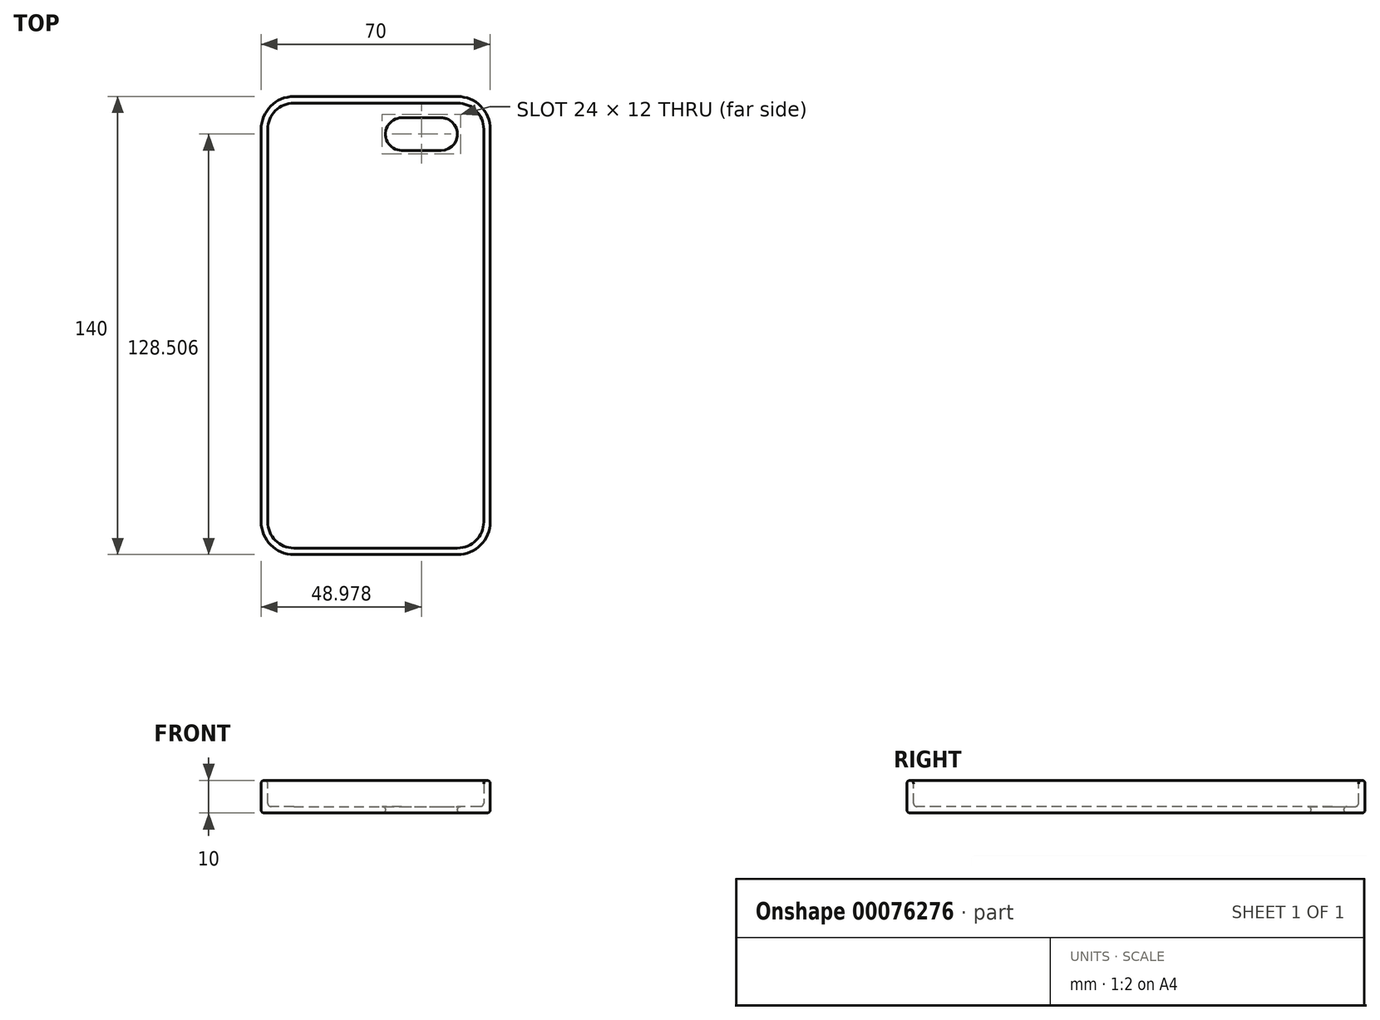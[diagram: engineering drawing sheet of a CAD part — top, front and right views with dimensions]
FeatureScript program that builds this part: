
annotation { "Feature Type Name" : "Feature", "Feature Type Description" : "" }
export const myFeature = defineFeature(function(context is Context, id is Id, definition is map)
    precondition{}
    {
        {
            var Q0;
            Q0=qCreatedBy(makeId("Top.planeOp"),FACE);
            var sketch = newSketch(context, id + "F0", { "sketchPlane" : qUnion([Q0])});
            skLineSegment(sketch, "E0.bottom", {"start": v(-23.57, 70.85) * mm, "end": v(26.43, 70.85) * mm});
            skLineSegment(sketch, "E0.top", {"start": v(-23.57, -69.15) * mm, "end": v(26.43, -69.15) * mm});
            skLineSegment(sketch, "E0.left", {"start": v(-33.57, 60.85) * mm, "end": v(-33.57, -59.15) * mm});
            skLineSegment(sketch, "E0.right", {"start": v(36.43, 60.85) * mm, "end": v(36.43, -59.15) * mm});
            skLineSegment(sketch, "E1.bottom", {"start": v(9.4, 64.36) * mm, "end": v(21.4, 64.36) * mm});
            skLineSegment(sketch, "E1.top", {"start": v(9.4, 54.36) * mm, "end": v(21.4, 54.36) * mm});
            skLineSegment(sketch, "E1.left", {"start": v(4.4, 59.36) * mm, "end": v(4.4, 59.36) * mm});
            skLineSegment(sketch, "E1.right", {"start": v(26.4, 59.36) * mm, "end": v(26.4, 59.36) * mm});
            skLineSegment(sketch, "E2.0", {"start": v(-23.38, 68.85) * mm, "end": v(26.84, 68.85) * mm});
            skLineSegment(sketch, "E3.0", {"start": v(-31.57, 60.76) * mm, "end": v(-31.57, -59.38) * mm});
            skLineSegment(sketch, "E4.0", {"start": v(-23.6, -67.15) * mm, "end": v(26.43, -67.15) * mm});
            skLineSegment(sketch, "E5.0", {"start": v(34.43, 60.88) * mm, "end": v(34.43, -59.15) * mm});
            skPoint(sketch, "E6.visualSharp", {"position": v(-33.57, 70.85) * mm});
            skArc(sketch, "E6.filletArc", {"start": v(-23.57, 70.85) * mm, "mid": v(-30.64, 67.92) * mm, "end": v(-33.57, 60.85) * mm});
            skPoint(sketch, "E7.visualSharp", {"position": v(36.43, 70.85) * mm});
            skArc(sketch, "E7.filletArc", {"start": v(36.43, 60.85) * mm, "mid": v(33.5, 67.92) * mm, "end": v(26.43, 70.85) * mm});
            skPoint(sketch, "E8.visualSharp", {"position": v(36.43, -69.15) * mm});
            skArc(sketch, "E8.filletArc", {"start": v(26.43, -69.15) * mm, "mid": v(33.5, -66.22) * mm, "end": v(36.43, -59.15) * mm});
            skPoint(sketch, "E9.visualSharp", {"position": v(-33.57, -69.15) * mm});
            skArc(sketch, "E9.filletArc", {"start": v(-33.57, -59.15) * mm, "mid": v(-30.64, -66.22) * mm, "end": v(-23.57, -69.15) * mm});
            skPoint(sketch, "E10.visualSharp", {"position": v(4.4, 54.36) * mm});
            skArc(sketch, "E10.filletArc", {"start": v(4.4, 59.36) * mm, "mid": v(5.87, 55.82) * mm, "end": v(9.4, 54.36) * mm});
            skPoint(sketch, "E11.visualSharp", {"position": v(4.4, 64.36) * mm});
            skArc(sketch, "E11.filletArc", {"start": v(9.4, 64.36) * mm, "mid": v(5.87, 62.9) * mm, "end": v(4.4, 59.36) * mm});
            skPoint(sketch, "E12.visualSharp", {"position": v(26.4, 64.36) * mm});
            skArc(sketch, "E12.filletArc", {"start": v(26.4, 59.36) * mm, "mid": v(24.94, 62.9) * mm, "end": v(21.4, 64.36) * mm});
            skPoint(sketch, "E13.visualSharp", {"position": v(26.4, 54.36) * mm});
            skArc(sketch, "E13.filletArc", {"start": v(21.4, 54.36) * mm, "mid": v(24.94, 55.82) * mm, "end": v(26.4, 59.36) * mm});
            skSolve(sketch);
        }
        {
            var Q0;
            Q0=makeQuery(id+"F0.imprint","IMPRINT",FACE,{"disambiguationData":[TD([[makeQuery(id+"F0.imprint","IMPRINT",EDGE,{"derivedFrom":sQuery(id+"F0.wireOp",EDGE,"E1.bottom")}),1.0]])]});
            extrude(context, id + "F1", {"entities" : qUnion([Q0]), "depth" : 2 * mm});
        }
        {
            var Q0;
            {var subQ0=sQuery(id+"F0.wireOp",EDGE,"E0.left");var subQ1=sQuery(id+"F0.wireOp",EDGE,"E0.bottom");var subQ2=makeQuery(id+"F0.imprint","INTERSECT",VERTEX,{"derivedFrom":[subQ1,subQ0]});Q0=makeQuery(id+"F0.imprint","IMPRINT",FACE,{"disambiguationData":[TD([[makeQuery(id+"F0.imprint","IMPRINT",EDGE,{"disambiguationData":[TD([[subQ2,-1.0]])],"derivedFrom":subQ1}),-1.0]])]});}
            var Q1;
            {var subQ0=sQuery(id+"F0.wireOp",EDGE,"E3.0");var subQ1=sQuery(id+"F0.wireOp",EDGE,"E0.bottom");var subQ2=makeQuery(id+"F0.imprint","INTERSECT",VERTEX,{"derivedFrom":[subQ1,subQ0]});Q1=makeQuery(id+"F0.imprint","IMPRINT",FACE,{"disambiguationData":[TD([[makeQuery(id+"F0.imprint","IMPRINT",EDGE,{"disambiguationData":[TD([[subQ2,-1.0]])],"derivedFrom":subQ1}),-1.0]])]});}
            var Q2;
            {var subQ0=sQuery(id+"F0.wireOp",EDGE,"E2.0");var subQ1=sQuery(id+"F0.wireOp",EDGE,"E0.left");var subQ2=makeQuery(id+"F0.imprint","INTERSECT",VERTEX,{"derivedFrom":[subQ1,subQ0]});Q2=makeQuery(id+"F0.imprint","IMPRINT",FACE,{"disambiguationData":[TD([[makeQuery(id+"F0.imprint","IMPRINT",EDGE,{"disambiguationData":[TD([[subQ2,-1.0]])],"derivedFrom":subQ1}),1.0]])]});}
            var Q3;
            {var subQ0=sQuery(id+"F0.wireOp",EDGE,"E0.left");var subQ1=sQuery(id+"F0.wireOp",EDGE,"E0.top");var subQ2=makeQuery(id+"F0.imprint","INTERSECT",VERTEX,{"derivedFrom":[subQ1,subQ0]});Q3=makeQuery(id+"F0.imprint","IMPRINT",FACE,{"disambiguationData":[TD([[makeQuery(id+"F0.imprint","IMPRINT",EDGE,{"disambiguationData":[TD([[subQ2,-1.0]])],"derivedFrom":subQ1}),1.0]])]});}
            var Q4;
            {var subQ0=sQuery(id+"F0.wireOp",EDGE,"E3.0");var subQ1=sQuery(id+"F0.wireOp",EDGE,"E0.top");var subQ2=makeQuery(id+"F0.imprint","INTERSECT",VERTEX,{"derivedFrom":[subQ1,subQ0]});Q4=makeQuery(id+"F0.imprint","IMPRINT",FACE,{"disambiguationData":[TD([[makeQuery(id+"F0.imprint","IMPRINT",EDGE,{"disambiguationData":[TD([[subQ2,-1.0]])],"derivedFrom":subQ1}),1.0]])]});}
            var Q5;
            {var subQ0=sQuery(id+"F0.wireOp",EDGE,"E2.0");var subQ1=sQuery(id+"F0.wireOp",EDGE,"E0.right");var subQ2=makeQuery(id+"F0.imprint","INTERSECT",VERTEX,{"derivedFrom":[subQ1,subQ0]});Q5=makeQuery(id+"F0.imprint","IMPRINT",FACE,{"disambiguationData":[TD([[makeQuery(id+"F0.imprint","IMPRINT",EDGE,{"disambiguationData":[TD([[subQ2,-1.0]])],"derivedFrom":subQ1}),-1.0]])]});}
            var Q6;
            {var subQ0=sQuery(id+"F0.wireOp",EDGE,"E0.right");var subQ1=sQuery(id+"F0.wireOp",EDGE,"E0.top");var subQ2=makeQuery(id+"F0.imprint","INTERSECT",VERTEX,{"derivedFrom":[subQ1,subQ0]});Q6=makeQuery(id+"F0.imprint","IMPRINT",FACE,{"disambiguationData":[TD([[makeQuery(id+"F0.imprint","IMPRINT",EDGE,{"disambiguationData":[TD([[subQ2,1.0]])],"derivedFrom":subQ1}),1.0]])]});}
            var Q7;
            {var subQ0=sQuery(id+"F0.wireOp",EDGE,"E0.right");var subQ1=sQuery(id+"F0.wireOp",EDGE,"E0.bottom");var subQ2=makeQuery(id+"F0.imprint","INTERSECT",VERTEX,{"derivedFrom":[subQ1,subQ0]});Q7=makeQuery(id+"F0.imprint","IMPRINT",FACE,{"disambiguationData":[TD([[makeQuery(id+"F0.imprint","IMPRINT",EDGE,{"disambiguationData":[TD([[subQ2,1.0]])],"derivedFrom":subQ1}),-1.0]])]});}
            extrude(context, id + "F2", {"entities" : qUnion([Q0, Q1, Q2, Q3, Q4, Q5, Q6, Q7]), "operationType" : NewBodyOperationType.ADD, "depth" : 10 * mm});
        }
        {
            var Q0;
            Q0=makeQuery(id+"F2.opExtrude","CAP_EDGE",EDGE,{"disambiguationData":[OSD([sQuery(id+"F0.wireOp",EDGE,"E0.left")])],"isStart":false});
            var Q1;
            Q1=makeQuery(id+"F2.opExtrude","CAP_EDGE",EDGE,{"disambiguationData":[OSD([sQuery(id+"F0.wireOp",EDGE,"E3.0")])],"isStart":false});
            var Q2;
            Q2=makeQuery(id+"F2.opExtrude","CAP_EDGE",EDGE,{"disambiguationData":[OSD([sQuery(id+"F0.wireOp",EDGE,"E2.0")])],"isStart":false});
            var Q3;
            Q3=makeQuery(id+"F2.opExtrude","CAP_EDGE",EDGE,{"disambiguationData":[OSD([sQuery(id+"F0.wireOp",EDGE,"E0.bottom")])],"isStart":false});
            var Q4;
            Q4=makeQuery(id+"F1.opExtrude","CAP_EDGE",EDGE,{"disambiguationData":[OSD([sQuery(id+"F0.wireOp",EDGE,"E1.bottom")])],"isStart":false});
            var Q5;
            Q5=makeQuery(id+"F1.opExtrude","CAP_EDGE",EDGE,{"disambiguationData":[OSD([sQuery(id+"F0.wireOp",EDGE,"E1.left")])],"isStart":false});
            var Q6;
            Q6=makeQuery(id+"F1.opExtrude","CAP_EDGE",EDGE,{"disambiguationData":[OSD([sQuery(id+"F0.wireOp",EDGE,"E1.right")])],"isStart":false});
            var Q7;
            Q7=makeQuery(id+"F1.opExtrude","CAP_EDGE",EDGE,{"disambiguationData":[OSD([sQuery(id+"F0.wireOp",EDGE,"E1.top")])],"isStart":false});
            var Q8;
            Q8=makeQuery(id+"F2.opExtrude","CAP_EDGE",EDGE,{"disambiguationData":[OSD([sQuery(id+"F0.wireOp",EDGE,"E5.0")])],"isStart":false});
            var Q9;
            Q9=makeQuery(id+"F2.opExtrude","CAP_EDGE",EDGE,{"disambiguationData":[OSD([sQuery(id+"F0.wireOp",EDGE,"E0.right")])],"isStart":false});
            var Q10;
            Q10=makeQuery(id+"F2.opExtrude","CAP_EDGE",EDGE,{"disambiguationData":[OSD([sQuery(id+"F0.wireOp",EDGE,"E4.0")])],"isStart":false});
            var Q11;
            Q11=makeQuery(id+"F2.opExtrude","CAP_EDGE",EDGE,{"disambiguationData":[OSD([sQuery(id+"F0.wireOp",EDGE,"E0.top")])],"isStart":false});
            fillet(context, id + "F3", {"entities" : qUnion([Q0, Q1, Q2, Q3, Q4, Q5, Q6, Q7, Q8, Q9, Q10, Q11]), "radius" : 1 * mm, "tangentPropagation" : true, "allowEdgeOverflow" : false});
        }
        {
            var Q0;
            Q0=makeQuery(id+"F2.opExtrude","CAP_EDGE",EDGE,{"disambiguationData":[OSD([sQuery(id+"F0.wireOp",EDGE,"E0.left")])],"isStart":true});
            var Q1;
            Q1=makeQuery(id+"F2.opExtrude","CAP_EDGE",EDGE,{"disambiguationData":[OSD([sQuery(id+"F0.wireOp",EDGE,"E0.top")])],"isStart":true});
            var Q2;
            Q2=makeQuery(id+"F2.opExtrude","CAP_EDGE",EDGE,{"disambiguationData":[OSD([sQuery(id+"F0.wireOp",EDGE,"E0.right")])],"isStart":true});
            var Q3;
            Q3=makeQuery(id+"F2.opExtrude","CAP_EDGE",EDGE,{"disambiguationData":[OSD([sQuery(id+"F0.wireOp",EDGE,"E0.bottom")])],"isStart":true});
            var Q4;
            Q4=makeQuery(id+"F1.opExtrude","CAP_EDGE",EDGE,{"disambiguationData":[OSD([sQuery(id+"F0.wireOp",EDGE,"E1.top")])],"isStart":true});
            var Q5;
            Q5=makeQuery(id+"F1.opExtrude","CAP_EDGE",EDGE,{"disambiguationData":[OSD([sQuery(id+"F0.wireOp",EDGE,"E1.left")])],"isStart":true});
            var Q6;
            Q6=makeQuery(id+"F1.opExtrude","CAP_EDGE",EDGE,{"disambiguationData":[OSD([sQuery(id+"F0.wireOp",EDGE,"E1.right")])],"isStart":true});
            var Q7;
            Q7=makeQuery(id+"F1.opExtrude","CAP_EDGE",EDGE,{"disambiguationData":[OSD([sQuery(id+"F0.wireOp",EDGE,"E1.bottom")])],"isStart":true});
            fillet(context, id + "F4", {"entities" : qUnion([Q0, Q1, Q2, Q3, Q4, Q5, Q6, Q7]), "radius" : 1 * mm, "tangentPropagation" : true, "allowEdgeOverflow" : false});
        }
        {
            var Q0;
            {var subQ0=sQuery(id+"F0.wireOp",EDGE,"E11.filletArc");var subQ1=sQuery(id+"F0.wireOp",EDGE,"E10.filletArc");Q0=makeQuery(id+"F2.boolean.opBoolean","MERGE",FACE,{"derivedFrom":[makeQuery(id+"F1.opExtrude","SWEPT_FACE",FACE,{"disambiguationData":[OSD([subQ1,subQ0])]}),makeQuery(id+"F2.opExtrude","SWEPT_FACE",FACE,{"disambiguationData":[OSD([subQ1,subQ0])]})]});}
            var Q1;
            {var subQ0=sQuery(id+"F0.wireOp",EDGE,"E1.bottom");Q1=makeQuery(id+"F2.boolean.opBoolean","MERGE",FACE,{"derivedFrom":[makeQuery(id+"F1.opExtrude","SWEPT_FACE",FACE,{"disambiguationData":[OSD([subQ0])]}),makeQuery(id+"F2.opExtrude","SWEPT_FACE",FACE,{"disambiguationData":[OSD([subQ0])]})]});}
            var Q2;
            {var subQ0=sQuery(id+"F0.wireOp",EDGE,"E13.filletArc");var subQ1=sQuery(id+"F0.wireOp",EDGE,"E12.filletArc");Q2=makeQuery(id+"F2.boolean.opBoolean","MERGE",FACE,{"derivedFrom":[makeQuery(id+"F1.opExtrude","SWEPT_FACE",FACE,{"disambiguationData":[OSD([subQ1,subQ0])]}),makeQuery(id+"F2.opExtrude","SWEPT_FACE",FACE,{"disambiguationData":[OSD([subQ1,subQ0])]})]});}
            var Q3;
            {var subQ0=sQuery(id+"F0.wireOp",EDGE,"E1.top");Q3=makeQuery(id+"F2.boolean.opBoolean","MERGE",FACE,{"derivedFrom":[makeQuery(id+"F1.opExtrude","SWEPT_FACE",FACE,{"disambiguationData":[OSD([subQ0])]}),makeQuery(id+"F2.opExtrude","SWEPT_FACE",FACE,{"disambiguationData":[OSD([subQ0])]})]});}
            var Q4;
            Q4=makeQuery(id+"F2.opExtrude","CAP_FACE",FACE,{"disambiguationData":[OSD([sQuery(id+"F0.wireOp",EDGE,"E0.bottom"),sQuery(id+"F0.wireOp",EDGE,"E0.top"),sQuery(id+"F0.wireOp",EDGE,"E0.left"),sQuery(id+"F0.wireOp",EDGE,"E0.right"),sQuery(id+"F0.wireOp",EDGE,"E1.bottom"),sQuery(id+"F0.wireOp",EDGE,"E1.top"),sQuery(id+"F0.wireOp",EDGE,"E6.filletArc"),sQuery(id+"F0.wireOp",EDGE,"E7.filletArc"),sQuery(id+"F0.wireOp",EDGE,"E8.filletArc"),sQuery(id+"F0.wireOp",EDGE,"E9.filletArc"),sQuery(id+"F0.wireOp",EDGE,"E10.filletArc"),sQuery(id+"F0.wireOp",EDGE,"E11.filletArc"),sQuery(id+"F0.wireOp",EDGE,"E12.filletArc"),sQuery(id+"F0.wireOp",EDGE,"E13.filletArc")])],"isStart":false});
            shell(context, id + "F5", {"entities" : qUnion([Q0, Q1, Q2, Q3, Q4]), "thickness" : 2 * mm});
        }
        {
            var Q0;
            {var subQ0=sQuery(id+"F0.wireOp",EDGE,"E11.filletArc");var subQ1=sQuery(id+"F0.wireOp",EDGE,"E10.filletArc");var subQ2=makeQuery(id+"F1.opExtrude","CAP_EDGE",EDGE,{"disambiguationData":[OSD([subQ1,subQ0])],"isStart":true});var subQ3=sQuery(id+"F0.wireOp",EDGE,"E13.filletArc");var subQ4=sQuery(id+"F0.wireOp",EDGE,"E12.filletArc");var subQ5=sQuery(id+"F0.wireOp",EDGE,"E9.filletArc");var subQ6=sQuery(id+"F0.wireOp",EDGE,"E8.filletArc");var subQ7=sQuery(id+"F0.wireOp",EDGE,"E7.filletArc");var subQ8=sQuery(id+"F0.wireOp",EDGE,"E6.filletArc");var subQ9=sQuery(id+"F0.wireOp",EDGE,"E1.top");var subQ10=sQuery(id+"F0.wireOp",EDGE,"E1.bottom");var subQ11=sQuery(id+"F0.wireOp",EDGE,"E0.right");var subQ12=sQuery(id+"F0.wireOp",EDGE,"E0.left");var subQ13=sQuery(id+"F0.wireOp",EDGE,"E0.top");var subQ14=sQuery(id+"F0.wireOp",EDGE,"E0.bottom");Q0=makeQuery(id+"F5.opShell","OFFSET_EDGE",EDGE,{"disambiguationData":[OSD([subQ14,subQ13,subQ12,subQ11,subQ10,subQ9,subQ8,subQ7,subQ6,subQ5,subQ1,subQ0,subQ4,subQ3]),TDD([makeQuery(id+"F4.opFillet","BLEND_EDGE",EDGE,{"blendedFrom":[subQ2,makeQuery(id+"F1.opExtrude","CAP_FACE",FACE,{"disambiguationData":[OSD([subQ14,subQ13,subQ12,subQ11,subQ10,subQ9,subQ8,subQ7,subQ6,subQ5,subQ1,subQ0,subQ4,subQ3])],"isStart":true})],"blendedInto":[makeQuery(id+"F1.opExtrude","CAP_FACE",FACE,{"disambiguationData":[OSD([subQ14,subQ13,subQ12,subQ11,subQ10,subQ9,subQ8,subQ7,subQ6,subQ5,subQ1,subQ0,subQ4,subQ3])],"isStart":true})]}),makeQuery(id+"F4.opFillet","BLEND_EDGE",EDGE,{"blendedFrom":[subQ2,makeQuery(id+"F2.boolean.opBoolean","MERGE",FACE,{"derivedFrom":[makeQuery(id+"F1.opExtrude","SWEPT_FACE",FACE,{"disambiguationData":[OSD([subQ1,subQ0])]}),makeQuery(id+"F2.opExtrude","SWEPT_FACE",FACE,{"disambiguationData":[OSD([subQ1,subQ0])]})]})],"blendedInto":[makeQuery(id+"F2.boolean.opBoolean","MERGE",FACE,{"derivedFrom":[makeQuery(id+"F1.opExtrude","SWEPT_FACE",FACE,{"disambiguationData":[OSD([subQ1,subQ0])]}),makeQuery(id+"F2.opExtrude","SWEPT_FACE",FACE,{"disambiguationData":[OSD([subQ1,subQ0])]})]})]})])]});}
            var Q1;
            {var subQ0=sQuery(id+"F0.wireOp",EDGE,"E1.bottom");var subQ1=makeQuery(id+"F1.opExtrude","CAP_EDGE",EDGE,{"disambiguationData":[OSD([subQ0])],"isStart":true});var subQ2=sQuery(id+"F0.wireOp",EDGE,"E13.filletArc");var subQ3=sQuery(id+"F0.wireOp",EDGE,"E12.filletArc");var subQ4=sQuery(id+"F0.wireOp",EDGE,"E11.filletArc");var subQ5=sQuery(id+"F0.wireOp",EDGE,"E10.filletArc");var subQ6=sQuery(id+"F0.wireOp",EDGE,"E9.filletArc");var subQ7=sQuery(id+"F0.wireOp",EDGE,"E8.filletArc");var subQ8=sQuery(id+"F0.wireOp",EDGE,"E7.filletArc");var subQ9=sQuery(id+"F0.wireOp",EDGE,"E6.filletArc");var subQ10=sQuery(id+"F0.wireOp",EDGE,"E1.top");var subQ11=sQuery(id+"F0.wireOp",EDGE,"E0.right");var subQ12=sQuery(id+"F0.wireOp",EDGE,"E0.left");var subQ13=sQuery(id+"F0.wireOp",EDGE,"E0.top");var subQ14=sQuery(id+"F0.wireOp",EDGE,"E0.bottom");Q1=makeQuery(id+"F5.opShell","OFFSET_EDGE",EDGE,{"disambiguationData":[OSD([subQ14,subQ13,subQ12,subQ11,subQ0,subQ10,subQ9,subQ8,subQ7,subQ6,subQ5,subQ4,subQ3,subQ2]),TDD([makeQuery(id+"F4.opFillet","BLEND_EDGE",EDGE,{"blendedFrom":[subQ1,makeQuery(id+"F1.opExtrude","CAP_FACE",FACE,{"disambiguationData":[OSD([subQ14,subQ13,subQ12,subQ11,subQ0,subQ10,subQ9,subQ8,subQ7,subQ6,subQ5,subQ4,subQ3,subQ2])],"isStart":true})],"blendedInto":[makeQuery(id+"F1.opExtrude","CAP_FACE",FACE,{"disambiguationData":[OSD([subQ14,subQ13,subQ12,subQ11,subQ0,subQ10,subQ9,subQ8,subQ7,subQ6,subQ5,subQ4,subQ3,subQ2])],"isStart":true})]}),makeQuery(id+"F4.opFillet","BLEND_EDGE",EDGE,{"blendedFrom":[subQ1,makeQuery(id+"F2.boolean.opBoolean","MERGE",FACE,{"derivedFrom":[makeQuery(id+"F1.opExtrude","SWEPT_FACE",FACE,{"disambiguationData":[OSD([subQ0])]}),makeQuery(id+"F2.opExtrude","SWEPT_FACE",FACE,{"disambiguationData":[OSD([subQ0])]})]})],"blendedInto":[makeQuery(id+"F2.boolean.opBoolean","MERGE",FACE,{"derivedFrom":[makeQuery(id+"F1.opExtrude","SWEPT_FACE",FACE,{"disambiguationData":[OSD([subQ0])]}),makeQuery(id+"F2.opExtrude","SWEPT_FACE",FACE,{"disambiguationData":[OSD([subQ0])]})]})]})])]});}
            var Q2;
            {var subQ0=sQuery(id+"F0.wireOp",EDGE,"E1.top");var subQ1=makeQuery(id+"F1.opExtrude","CAP_EDGE",EDGE,{"disambiguationData":[OSD([subQ0])],"isStart":true});var subQ2=sQuery(id+"F0.wireOp",EDGE,"E13.filletArc");var subQ3=sQuery(id+"F0.wireOp",EDGE,"E12.filletArc");var subQ4=sQuery(id+"F0.wireOp",EDGE,"E11.filletArc");var subQ5=sQuery(id+"F0.wireOp",EDGE,"E10.filletArc");var subQ6=sQuery(id+"F0.wireOp",EDGE,"E9.filletArc");var subQ7=sQuery(id+"F0.wireOp",EDGE,"E8.filletArc");var subQ8=sQuery(id+"F0.wireOp",EDGE,"E7.filletArc");var subQ9=sQuery(id+"F0.wireOp",EDGE,"E6.filletArc");var subQ10=sQuery(id+"F0.wireOp",EDGE,"E1.bottom");var subQ11=sQuery(id+"F0.wireOp",EDGE,"E0.right");var subQ12=sQuery(id+"F0.wireOp",EDGE,"E0.left");var subQ13=sQuery(id+"F0.wireOp",EDGE,"E0.top");var subQ14=sQuery(id+"F0.wireOp",EDGE,"E0.bottom");Q2=makeQuery(id+"F5.opShell","OFFSET_EDGE",EDGE,{"disambiguationData":[OSD([subQ14,subQ13,subQ12,subQ11,subQ10,subQ0,subQ9,subQ8,subQ7,subQ6,subQ5,subQ4,subQ3,subQ2]),TDD([makeQuery(id+"F4.opFillet","BLEND_EDGE",EDGE,{"blendedFrom":[subQ1,makeQuery(id+"F1.opExtrude","CAP_FACE",FACE,{"disambiguationData":[OSD([subQ14,subQ13,subQ12,subQ11,subQ10,subQ0,subQ9,subQ8,subQ7,subQ6,subQ5,subQ4,subQ3,subQ2])],"isStart":true})],"blendedInto":[makeQuery(id+"F1.opExtrude","CAP_FACE",FACE,{"disambiguationData":[OSD([subQ14,subQ13,subQ12,subQ11,subQ10,subQ0,subQ9,subQ8,subQ7,subQ6,subQ5,subQ4,subQ3,subQ2])],"isStart":true})]}),makeQuery(id+"F4.opFillet","BLEND_EDGE",EDGE,{"blendedFrom":[subQ1,makeQuery(id+"F2.boolean.opBoolean","MERGE",FACE,{"derivedFrom":[makeQuery(id+"F1.opExtrude","SWEPT_FACE",FACE,{"disambiguationData":[OSD([subQ0])]}),makeQuery(id+"F2.opExtrude","SWEPT_FACE",FACE,{"disambiguationData":[OSD([subQ0])]})]})],"blendedInto":[makeQuery(id+"F2.boolean.opBoolean","MERGE",FACE,{"derivedFrom":[makeQuery(id+"F1.opExtrude","SWEPT_FACE",FACE,{"disambiguationData":[OSD([subQ0])]}),makeQuery(id+"F2.opExtrude","SWEPT_FACE",FACE,{"disambiguationData":[OSD([subQ0])]})]})]})])]});}
            var Q3;
            {var subQ0=sQuery(id+"F0.wireOp",EDGE,"E13.filletArc");var subQ1=sQuery(id+"F0.wireOp",EDGE,"E12.filletArc");var subQ2=makeQuery(id+"F1.opExtrude","CAP_EDGE",EDGE,{"disambiguationData":[OSD([subQ1,subQ0])],"isStart":true});var subQ3=sQuery(id+"F0.wireOp",EDGE,"E11.filletArc");var subQ4=sQuery(id+"F0.wireOp",EDGE,"E10.filletArc");var subQ5=sQuery(id+"F0.wireOp",EDGE,"E9.filletArc");var subQ6=sQuery(id+"F0.wireOp",EDGE,"E8.filletArc");var subQ7=sQuery(id+"F0.wireOp",EDGE,"E7.filletArc");var subQ8=sQuery(id+"F0.wireOp",EDGE,"E6.filletArc");var subQ9=sQuery(id+"F0.wireOp",EDGE,"E1.top");var subQ10=sQuery(id+"F0.wireOp",EDGE,"E1.bottom");var subQ11=sQuery(id+"F0.wireOp",EDGE,"E0.right");var subQ12=sQuery(id+"F0.wireOp",EDGE,"E0.left");var subQ13=sQuery(id+"F0.wireOp",EDGE,"E0.top");var subQ14=sQuery(id+"F0.wireOp",EDGE,"E0.bottom");Q3=makeQuery(id+"F5.opShell","OFFSET_EDGE",EDGE,{"disambiguationData":[OSD([subQ14,subQ13,subQ12,subQ11,subQ10,subQ9,subQ8,subQ7,subQ6,subQ5,subQ4,subQ3,subQ1,subQ0]),TDD([makeQuery(id+"F4.opFillet","BLEND_EDGE",EDGE,{"blendedFrom":[subQ2,makeQuery(id+"F1.opExtrude","CAP_FACE",FACE,{"disambiguationData":[OSD([subQ14,subQ13,subQ12,subQ11,subQ10,subQ9,subQ8,subQ7,subQ6,subQ5,subQ4,subQ3,subQ1,subQ0])],"isStart":true})],"blendedInto":[makeQuery(id+"F1.opExtrude","CAP_FACE",FACE,{"disambiguationData":[OSD([subQ14,subQ13,subQ12,subQ11,subQ10,subQ9,subQ8,subQ7,subQ6,subQ5,subQ4,subQ3,subQ1,subQ0])],"isStart":true})]}),makeQuery(id+"F4.opFillet","BLEND_EDGE",EDGE,{"blendedFrom":[subQ2,makeQuery(id+"F2.boolean.opBoolean","MERGE",FACE,{"derivedFrom":[makeQuery(id+"F1.opExtrude","SWEPT_FACE",FACE,{"disambiguationData":[OSD([subQ1,subQ0])]}),makeQuery(id+"F2.opExtrude","SWEPT_FACE",FACE,{"disambiguationData":[OSD([subQ1,subQ0])]})]})],"blendedInto":[makeQuery(id+"F2.boolean.opBoolean","MERGE",FACE,{"derivedFrom":[makeQuery(id+"F1.opExtrude","SWEPT_FACE",FACE,{"disambiguationData":[OSD([subQ1,subQ0])]}),makeQuery(id+"F2.opExtrude","SWEPT_FACE",FACE,{"disambiguationData":[OSD([subQ1,subQ0])]})]})]})])]});}
            var Q4;
            Q4=makeQuery(id+"F2.opExtrude","CAP_FACE",FACE,{"disambiguationData":[OSD([sQuery(id+"F0.wireOp",EDGE,"E0.bottom"),sQuery(id+"F0.wireOp",EDGE,"E0.top"),sQuery(id+"F0.wireOp",EDGE,"E0.left"),sQuery(id+"F0.wireOp",EDGE,"E0.right"),sQuery(id+"F0.wireOp",EDGE,"E1.bottom"),sQuery(id+"F0.wireOp",EDGE,"E1.top"),sQuery(id+"F0.wireOp",EDGE,"E6.filletArc"),sQuery(id+"F0.wireOp",EDGE,"E7.filletArc"),sQuery(id+"F0.wireOp",EDGE,"E8.filletArc"),sQuery(id+"F0.wireOp",EDGE,"E9.filletArc"),sQuery(id+"F0.wireOp",EDGE,"E10.filletArc"),sQuery(id+"F0.wireOp",EDGE,"E11.filletArc"),sQuery(id+"F0.wireOp",EDGE,"E12.filletArc"),sQuery(id+"F0.wireOp",EDGE,"E13.filletArc")])],"isStart":false});
            fillet(context, id + "F6", {"entities" : qUnion([Q0, Q1, Q2, Q3, Q4]), "radius" : 1 * mm, "tangentPropagation" : true, "allowEdgeOverflow" : false});
        }
        {
            var Q0;
            Q0=makeQuery(id+"F1.opExtrude","CAP_EDGE",EDGE,{"disambiguationData":[OSD([sQuery(id+"F0.wireOp",EDGE,"E9.filletArc")])],"isStart":true});
            var Q1;
            Q1=makeQuery(id+"F1.opExtrude","CAP_EDGE",EDGE,{"disambiguationData":[OSD([sQuery(id+"F0.wireOp",EDGE,"E0.top")])],"isStart":true});
            var Q2;
            Q2=makeQuery(id+"F1.opExtrude","CAP_EDGE",EDGE,{"disambiguationData":[OSD([sQuery(id+"F0.wireOp",EDGE,"E0.left")])],"isStart":true});
            var Q3;
            Q3=makeQuery(id+"F1.opExtrude","CAP_EDGE",EDGE,{"disambiguationData":[OSD([sQuery(id+"F0.wireOp",EDGE,"E0.right")])],"isStart":true});
            var Q4;
            Q4=makeQuery(id+"F1.opExtrude","CAP_EDGE",EDGE,{"disambiguationData":[OSD([sQuery(id+"F0.wireOp",EDGE,"E8.filletArc")])],"isStart":true});
            var Q5;
            Q5=makeQuery(id+"F1.opExtrude","CAP_EDGE",EDGE,{"disambiguationData":[OSD([sQuery(id+"F0.wireOp",EDGE,"E7.filletArc")])],"isStart":true});
            var Q6;
            Q6=makeQuery(id+"F1.opExtrude","CAP_EDGE",EDGE,{"disambiguationData":[OSD([sQuery(id+"F0.wireOp",EDGE,"E0.bottom")])],"isStart":true});
            var Q7;
            Q7=makeQuery(id+"F1.opExtrude","CAP_EDGE",EDGE,{"disambiguationData":[OSD([sQuery(id+"F0.wireOp",EDGE,"E6.filletArc")])],"isStart":true});
            fillet(context, id + "F7", {"entities" : qUnion([Q0, Q1, Q2, Q3, Q4, Q5, Q6, Q7]), "radius" : 1 * mm, "tangentPropagation" : true, "allowEdgeOverflow" : false});
        }
        {
            var Q0;
            Q0=makeQuery(id+"F5.opShell","OFFSET_EDGE",EDGE,{"disambiguationData":[OSD([sQuery(id+"F0.wireOp",EDGE,"E6.filletArc")])]});
            var Q1;
            Q1=makeQuery(id+"F5.opShell","OFFSET_EDGE",EDGE,{"disambiguationData":[OSD([sQuery(id+"F0.wireOp",EDGE,"E0.bottom")])]});
            var Q2;
            Q2=makeQuery(id+"F5.opShell","OFFSET_EDGE",EDGE,{"disambiguationData":[OSD([sQuery(id+"F0.wireOp",EDGE,"E0.left")])]});
            var Q3;
            Q3=makeQuery(id+"F5.opShell","OFFSET_EDGE",EDGE,{"disambiguationData":[OSD([sQuery(id+"F0.wireOp",EDGE,"E7.filletArc")])]});
            var Q4;
            Q4=makeQuery(id+"F5.opShell","OFFSET_EDGE",EDGE,{"disambiguationData":[OSD([sQuery(id+"F0.wireOp",EDGE,"E0.right")])]});
            var Q5;
            Q5=makeQuery(id+"F5.opShell","OFFSET_EDGE",EDGE,{"disambiguationData":[OSD([sQuery(id+"F0.wireOp",EDGE,"E8.filletArc")])]});
            var Q6;
            Q6=makeQuery(id+"F5.opShell","OFFSET_EDGE",EDGE,{"disambiguationData":[OSD([sQuery(id+"F0.wireOp",EDGE,"E0.top")])]});
            var Q7;
            Q7=makeQuery(id+"F5.opShell","OFFSET_EDGE",EDGE,{"disambiguationData":[OSD([sQuery(id+"F0.wireOp",EDGE,"E9.filletArc")])]});
            fillet(context, id + "F8", {"entities" : qUnion([Q0, Q1, Q2, Q3, Q4, Q5, Q6, Q7]), "radius" : 1 * mm, "tangentPropagation" : true, "allowEdgeOverflow" : false});
        }
    });
